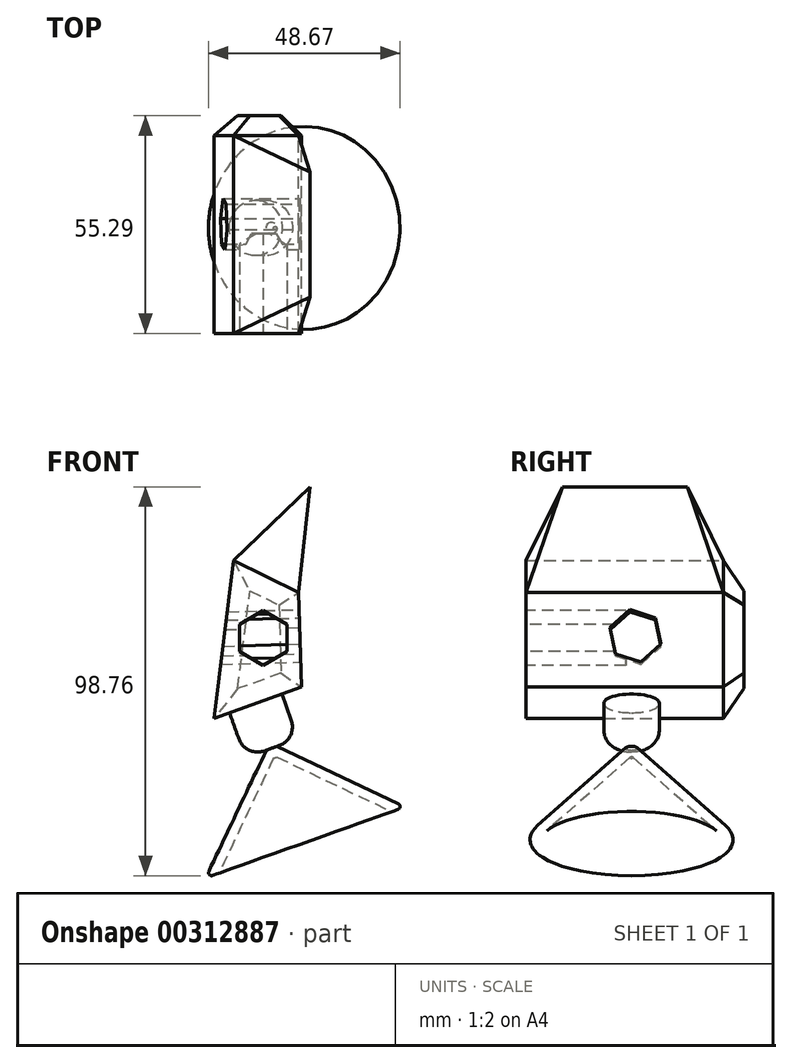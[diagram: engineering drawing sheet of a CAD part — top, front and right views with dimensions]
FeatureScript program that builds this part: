
annotation { "Feature Type Name" : "Feature", "Feature Type Description" : "" }
export const myFeature = defineFeature(function(context is Context, id is Id, definition is map)
    precondition{}
    {
        {
            var Q0;
            Q0=qCreatedBy(makeId("Front.planeOp"),FACE);
            var sketch = newSketch(context, id + "F0", { "sketchPlane" : qUnion([Q0])});
            skLineSegment(sketch, "E0", {"start": v(-13.71, 43.48) * mm, "end": v(-35.95, 35.55) * mm});
            skLineSegment(sketch, "E1", {"start": v(-35.95, 35.55) * mm, "end": v(-30.95, 75.67) * mm});
            skLineSegment(sketch, "E2", {"start": v(-30.95, 75.67) * mm, "end": v(-14.4, 67.55) * mm});
            skLineSegment(sketch, "E3", {"start": v(-14.4, 67.55) * mm, "end": v(-13.71, 43.48) * mm});
            skSolve(sketch);
        }
        {
            var Q0;
            Q0 = qSketchRegion(id + "F0", true);
            extrude(context, id + "F1", {"entities" : qUnion([Q0]), "depth" : 55.3 * mm});
        }
        {
            var Q0;
            Q0=makeQuery(id+"F1.opExtrude","SWEPT_FACE",FACE,{"disambiguationData":[OSD([sQuery(id+"F0.wireOp",EDGE,"E0")])]});
            var sketch = newSketch(context, id + "F2", { "sketchPlane" : qUnion([Q0])});
            skCircle(sketch, "E4", {"center": v(-10.62, 28.48) * mm, "radius": 7.08 * mm});
            skSolve(sketch);
        }
        {
            var Q0;
            Q0 = qSketchRegion(id + "F2", true);
            extrude(context, id + "F3", {"entities" : qUnion([Q0]), "operationType" : NewBodyOperationType.ADD, "depth" : 12.1 * mm});
        }
        {
            var Q0;
            Q0=makeQuery(id+"F3.opExtrude","CAP_EDGE",EDGE,{"disambiguationData":[OSD([sQuery(id+"F2.wireOp",EDGE,"E4")])],"isStart":false});
            fillet(context, id + "F4", {"entities" : qUnion([Q0]), "radius" : 5.08 * mm, "tangentPropagation" : true, "allowEdgeOverflow" : false});
        }
        {
            var Q0;
            Q0=makeQuery(id+"F1.opExtrude","SWEPT_FACE",FACE,{"disambiguationData":[OSD([sQuery(id+"F0.wireOp",EDGE,"E3")])]});
            var sketch = newSketch(context, id + "F5", { "sketchPlane" : qUnion([Q0])});
            skCircle(sketch, "E5.cCircle", {"center": v(-27.5, 56.89) * mm, "radius": 5.88 * mm, "construction": true});
            skLineSegment(sketch, "E5.0", {"start": v(-33.97, 59) * mm, "end": v(-28.91, 63.54) * mm});
            skLineSegment(sketch, "E5.1", {"start": v(-28.91, 63.54) * mm, "end": v(-22.45, 61.43) * mm});
            skLineSegment(sketch, "E5.2", {"start": v(-22.45, 61.43) * mm, "end": v(-21.05, 54.78) * mm});
            skLineSegment(sketch, "E5.3", {"start": v(-21.05, 54.78) * mm, "end": v(-26.1, 50.24) * mm});
            skLineSegment(sketch, "E5.4", {"start": v(-26.1, 50.24) * mm, "end": v(-32.56, 52.35) * mm});
            skLineSegment(sketch, "E5.5", {"start": v(-32.56, 52.35) * mm, "end": v(-33.97, 59) * mm});
            skPoint(sketch, "E5.0.midPoint", {"position": v(-31.44, 61.27) * mm});
            skSolve(sketch);
        }
        {
            var Q0;
            Q0 = qSketchRegion(id + "F5", true);
            extrude(context, id + "F6", {"entities" : qUnion([Q0]), "operationType" : NewBodyOperationType.REMOVE, "oppositeDirection" : true, "depth" : 25.4 * mm});
        }
        {
            var Q0;
            Q0=makeQuery(id+"F1.opExtrude","CAP_EDGE",EDGE,{"disambiguationData":[OSD([sQuery(id+"F0.wireOp",EDGE,"E3")])],"isStart":true});
            var Q1;
            Q1=makeQuery(id+"F1.opExtrude","CAP_EDGE",EDGE,{"disambiguationData":[OSD([sQuery(id+"F0.wireOp",EDGE,"E0")])],"isStart":true});
            var Q2;
            Q2=makeQuery(id+"F1.opExtrude","CAP_EDGE",EDGE,{"disambiguationData":[OSD([sQuery(id+"F0.wireOp",EDGE,"E2")])],"isStart":true});
            var Q3;
            Q3=makeQuery(id+"F1.opExtrude","CAP_EDGE",EDGE,{"disambiguationData":[OSD([sQuery(id+"F0.wireOp",EDGE,"E1")])],"isStart":true});
            chamfer(context, id + "F7", {"entities" : qUnion([Q0, Q1, Q2, Q3]), "width" : 5.08 * mm, "tangentPropagation" : true});
        }
        {
            var Q0;
            Q0=makeQuery(id+"F1.opExtrude","CAP_FACE",FACE,{"disambiguationData":[OSD([sQuery(id+"F0.wireOp",EDGE,"E0"),sQuery(id+"F0.wireOp",EDGE,"E1"),sQuery(id+"F0.wireOp",EDGE,"E2"),sQuery(id+"F0.wireOp",EDGE,"E3")])],"isStart":false});
            var sketch = newSketch(context, id + "F8", { "sketchPlane" : qUnion([Q0])});
            skCircle(sketch, "E6.cCircle", {"center": v(-23.41, 55.98) * mm, "radius": 6 * mm, "construction": true});
            skLineSegment(sketch, "E6.0", {"start": v(-29.42, 52.51) * mm, "end": v(-29.42, 59.45) * mm});
            skLineSegment(sketch, "E6.1", {"start": v(-29.42, 59.45) * mm, "end": v(-23.41, 62.92) * mm});
            skLineSegment(sketch, "E6.2", {"start": v(-23.41, 62.92) * mm, "end": v(-17.4, 59.45) * mm});
            skLineSegment(sketch, "E6.3", {"start": v(-17.4, 59.45) * mm, "end": v(-17.4, 52.51) * mm});
            skLineSegment(sketch, "E6.4", {"start": v(-17.4, 52.51) * mm, "end": v(-23.41, 49.04) * mm});
            skLineSegment(sketch, "E6.5", {"start": v(-23.41, 49.04) * mm, "end": v(-29.42, 52.51) * mm});
            skPoint(sketch, "E6.0.midPoint", {"position": v(-29.42, 55.98) * mm});
            skSolve(sketch);
        }
        {
            var Q0;
            Q0 = qSketchRegion(id + "F8", true);
            extrude(context, id + "F9", {"entities" : qUnion([Q0]), "operationType" : NewBodyOperationType.REMOVE, "oppositeDirection" : true, "depth" : 25.4 * mm});
        }
        {
            var Q0;
            Q0=makeQuery(id+"F3.opExtrude","CAP_FACE",FACE,{"disambiguationData":[OSD([sQuery(id+"F2.wireOp",EDGE,"E4")])],"isStart":false});
            var sketch = newSketch(context, id + "F10", { "sketchPlane" : qUnion([Q0])});
            skCircle(sketch, "E7", {"center": v(-10.62, 28.48) * mm, "radius": 1.47 * mm});
            skSolve(sketch);
        }
        {
            var Q0;
            Q0 = qSketchRegion(id + "F10", true);
            extrude(context, id + "F11", {"entities" : qUnion([Q0]), "depth" : 25.4 * mm, "hasDraft" : true, "draftAngle" : 45 * degree});
        }
        {
            var Q0;
            Q0=makeQuery(id+"F11.opExtrude","CAP_FACE",FACE,{"disambiguationData":[OSD([sQuery(id+"F10.wireOp",EDGE,"E7")])],"isStart":false});
            shell(context, id + "F12", {"entities" : qUnion([Q0]), "thickness" : 2.54 * mm});
        }
        {
            var Q0;
            Q0=makeQuery(id+"F11.opExtrude","CAP_EDGE",EDGE,{"disambiguationData":[OSD([sQuery(id+"F10.wireOp",EDGE,"E7")])],"isStart":false});
            fillet(context, id + "F13", {"entities" : qUnion([Q0]), "radius" : 0.76 * mm, "tangentPropagation" : true, "allowEdgeOverflow" : false});
        }
        {
            var Q0;
            {var subQ0=sQuery(id+"F10.wireOp",EDGE,"E7");Q0=makeQuery(id+"F12.opShell","OFFSET_EDGE",EDGE,{"disambiguationData":[OSD([subQ0]),TDD([makeQuery(id+"F11.opExtrude","CAP_EDGE",EDGE,{"disambiguationData":[OSD([subQ0])],"isStart":false})])]});}
            fillet(context, id + "F14", {"entities" : qUnion([Q0]), "radius" : 0.76 * mm, "tangentPropagation" : true, "allowEdgeOverflow" : false});
        }
        {
            var Q0;
            Q0=makeQuery(id+"F1.opExtrude","SWEPT_FACE",FACE,{"disambiguationData":[OSD([sQuery(id+"F0.wireOp",EDGE,"E2")])]});
            extrude(context, id + "F15", {"entities" : qUnion([Q0]), "operationType" : NewBodyOperationType.ADD, "depth" : 25.4 * mm, "hasDraft" : true, "draftAngle" : 20 * degree, "draftPullDirection" : true});
        }
    });
